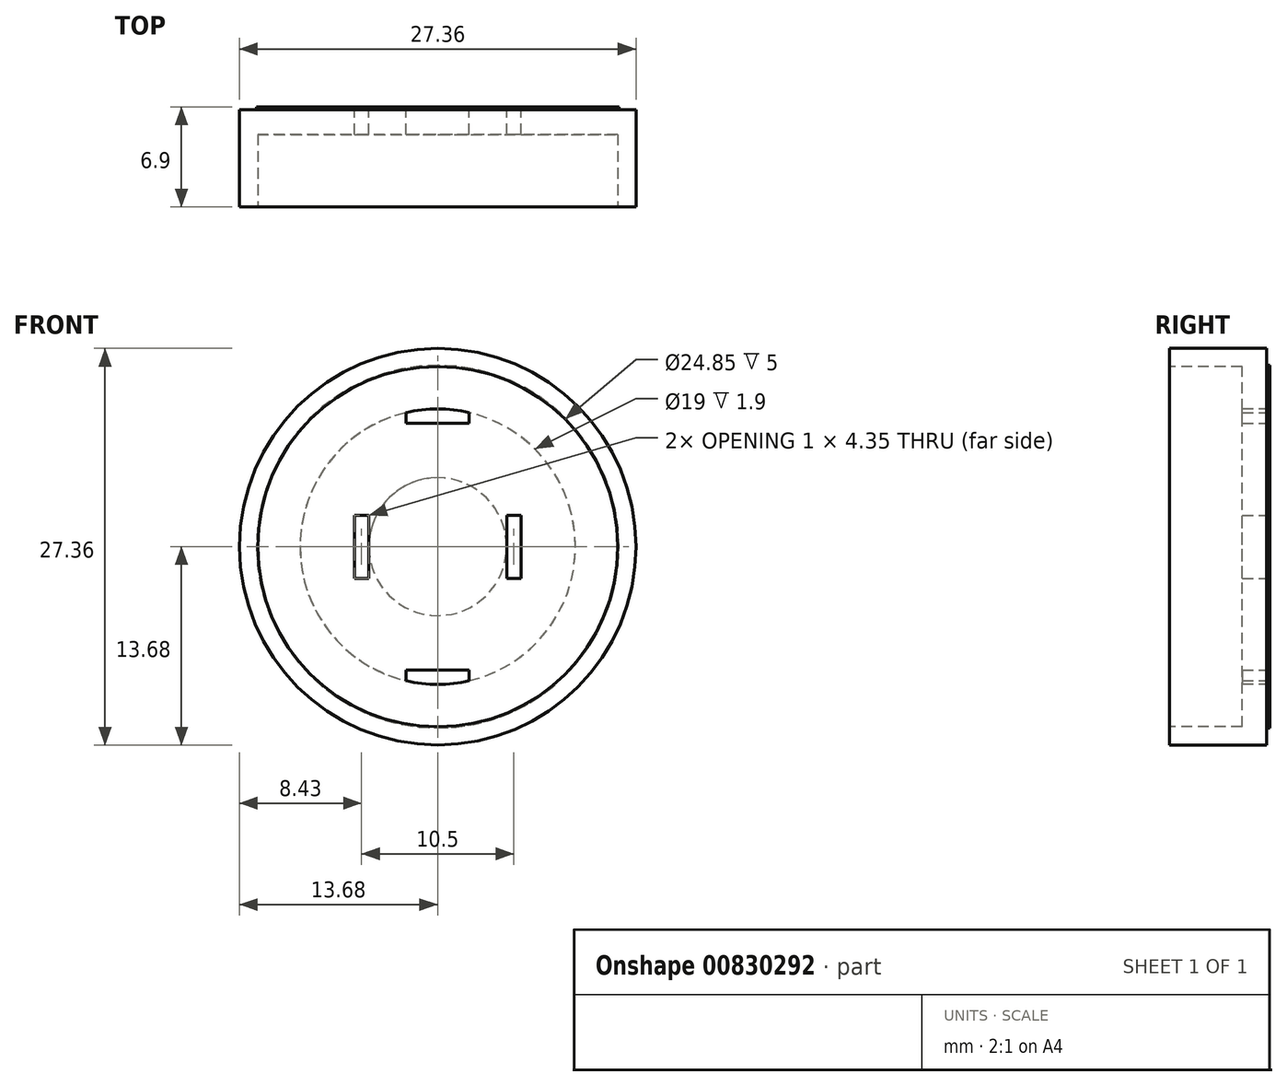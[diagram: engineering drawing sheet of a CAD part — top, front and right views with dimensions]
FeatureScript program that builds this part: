
annotation { "Feature Type Name" : "Feature", "Feature Type Description" : "" }
export const myFeature = defineFeature(function(context is Context, id is Id, definition is map)
    precondition{}
    {
        {
            var Q0;
            Q0=qCreatedBy(makeId("Front.planeOp"),FACE);
            var sketch = newSketch(context, id + "F0", { "sketchPlane" : qUnion([Q0])});
            skCircle(sketch, "E0", {"center": v(0, 0) * mm, "radius": 13.68 * mm});
            skSolve(sketch);
        }
        {
            var Q0;
            Q0 = qSketchRegion(id + "F0", true);
            extrude(context, id + "F1", {"entities" : qUnion([Q0]), "depth" : 6.7 * mm, "offsetDistance" : 25 * mm});
        }
        {
            var Q0;
            Q0=makeQuery(id+"F1.opExtrude","CAP_FACE",FACE,{"disambiguationData":[OSD([sQuery(id+"F0.wireOp",EDGE,"E0")])],"isStart":false});
            var sketch = newSketch(context, id + "F2", { "sketchPlane" : qUnion([Q0])});
            skCircle(sketch, "E1", {"center": v(0, 0) * mm, "radius": 12.43 * mm});
            skSolve(sketch);
        }
        {
            var Q0;
            Q0=makeQuery(id+"F2.imprint","IMPRINT",FACE,{"disambiguationData":[TD([[makeQuery(id+"F2.imprint","IMPRINT",EDGE,{"derivedFrom":sQuery(id+"F2.wireOp",EDGE,"E1")}),1.0]])]});
            extrude(context, id + "F3", {"entities" : qUnion([Q0]), "operationType" : NewBodyOperationType.REMOVE, "oppositeDirection" : true, "depth" : 5 * mm, "offsetDistance" : 25 * mm});
        }
        {
            var Q0;
            Q0=makeQuery(id+"F1.opExtrude","CAP_FACE",FACE,{"disambiguationData":[OSD([sQuery(id+"F0.wireOp",EDGE,"E0")])],"isStart":true});
            var sketch = newSketch(context, id + "F4", { "sketchPlane" : qUnion([Q0])});
            skCircle(sketch, "E2", {"center": v(0, 0) * mm, "radius": 4.75 * mm});
            skCircle(sketch, "E3", {"center": v(0, 0) * mm, "radius": 9.5 * mm});
            skCircle(sketch, "E4", {"center": v(0, 0) * mm, "radius": 12.5 * mm});
            skSolve(sketch);
        }
        {
            var Q0;
            Q0=makeQuery(id+"F4.imprint","IMPRINT",FACE,{"disambiguationData":[TD([[makeQuery(id+"F4.imprint","IMPRINT",EDGE,{"derivedFrom":sQuery(id+"F4.wireOp",EDGE,"E2")}),1.0]])]});
            extrude(context, id + "F5", {"entities" : qUnion([Q0]), "operationType" : NewBodyOperationType.ADD, "depth" : 0.2 * mm, "offsetDistance" : 25 * mm});
        }
        {
            var Q0;
            Q0=makeQuery(id+"F4.imprint","IMPRINT",FACE,{"disambiguationData":[TD([[makeQuery(id+"F4.imprint","IMPRINT",EDGE,{"derivedFrom":sQuery(id+"F4.wireOp",EDGE,"E3")}),-1.0]])]});
            extrude(context, id + "F6", {"entities" : qUnion([Q0]), "operationType" : NewBodyOperationType.ADD, "depth" : 0.2 * mm, "offsetDistance" : 25 * mm});
        }
        {
            var Q0;
            Q0=makeQuery(id+"F4.imprint","IMPRINT",FACE,{"disambiguationData":[TD([[makeQuery(id+"F4.imprint","IMPRINT",EDGE,{"derivedFrom":sQuery(id+"F4.wireOp",EDGE,"E2")}),-1.0]])]});
            var sketch = newSketch(context, id + "F7", { "sketchPlane" : qUnion([Q0])});
            skLineSegment(sketch, "E5.bottom", {"start": v(4.75, 2.17) * mm, "end": v(5.75, 2.17) * mm});
            skLineSegment(sketch, "E5.top", {"start": v(4.75, -2.17) * mm, "end": v(5.75, -2.17) * mm});
            skLineSegment(sketch, "E5.left", {"start": v(4.75, 2.17) * mm, "end": v(4.75, -2.17) * mm});
            skLineSegment(sketch, "E5.right", {"start": v(5.75, 2.17) * mm, "end": v(5.75, -2.17) * mm});
            skLineSegment(sketch, "E6.1.0", {"start": v(-4.75, -2.18) * mm, "end": v(-5.75, -2.18) * mm});
            skLineSegment(sketch, "E6.1.1", {"start": v(-4.75, -2.18) * mm, "end": v(-4.75, 2.17) * mm});
            skLineSegment(sketch, "E6.1.2", {"start": v(-5.75, -2.18) * mm, "end": v(-5.75, 2.17) * mm});
            skLineSegment(sketch, "E6.1.3", {"start": v(-4.75, 2.17) * mm, "end": v(-5.75, 2.17) * mm});
            skPoint(sketch, "E6.center", {"position": v(0, 0) * mm});
            skLineSegment(sketch, "E6.anchor1", {"start": v(0, 0) * mm, "end": v(4.75, 2.17) * mm, "construction": true});
            skLineSegment(sketch, "E6.anchor2", {"start": v(0, 0) * mm, "end": v(-4.75, -2.18) * mm, "construction": true});
            skSolve(sketch);
        }
        {
            var Q0;
            {var subQ3=sQuery(id+"F7.wireOp",EDGE,"E6.1.0");Q0=makeQuery(id+"F7.imprint","IMPRINT",FACE,{"disambiguationData":[TD([[makeQuery(id+"F7.imprint","IMPRINT",EDGE,{"derivedFrom":subQ3}),-1.0]])]});}
            var Q1;
            {var subQ3=sQuery(id+"F7.wireOp",EDGE,"E5.bottom");Q1=makeQuery(id+"F7.imprint","IMPRINT",FACE,{"disambiguationData":[TD([[makeQuery(id+"F7.imprint","IMPRINT",EDGE,{"derivedFrom":subQ3}),-1.0]])]});}
            var Q2;
            Q2=sQuery(id+"F7.wireOp",EDGE,"E6.1.2");
            var Q3;
            Q3=sQuery(id+"F7.wireOp",EDGE,"E6.1.1");
            var Q4;
            Q4=sQuery(id+"F7.wireOp",EDGE,"E6.1.3");
            var Q5;
            Q5=sQuery(id+"F7.wireOp",EDGE,"E6.1.0");
            var Q6;
            Q6=sQuery(id+"F7.wireOp",EDGE,"E5.top");
            var Q7;
            Q7=sQuery(id+"F7.wireOp",EDGE,"E5.right");
            var Q8;
            Q8=sQuery(id+"F7.wireOp",EDGE,"E5.left");
            var Q9;
            Q9=sQuery(id+"F7.wireOp",EDGE,"E5.bottom");
            extrude(context, id + "F8", {"entities" : qUnion([Q0, Q1]), "operationType" : NewBodyOperationType.REMOVE, "surfaceEntities" : qUnion([Q2, Q3, Q4, Q5, Q6, Q7, Q8, Q9]), "endBound" : BoundingType.THROUGH_ALL, "oppositeDirection" : true, "depth" : 25 * mm, "offsetDistance" : 25 * mm});
        }
        {
            var Q0;
            Q0=makeQuery(id+"F4.imprint","IMPRINT",FACE,{"disambiguationData":[TD([[makeQuery(id+"F4.imprint","IMPRINT",EDGE,{"derivedFrom":sQuery(id+"F4.wireOp",EDGE,"E2")}),-1.0]])]});
            var sketch = newSketch(context, id + "F9", { "sketchPlane" : qUnion([Q0])});
            skLineSegment(sketch, "E7.bottom", {"start": v(-2.17, 9.5) * mm, "end": v(2.17, 9.5) * mm});
            skLineSegment(sketch, "E7.top", {"start": v(-2.17, 8.5) * mm, "end": v(2.17, 8.5) * mm});
            skLineSegment(sketch, "E7.left", {"start": v(-2.18, 9.5) * mm, "end": v(-2.18, 8.5) * mm});
            skLineSegment(sketch, "E7.right", {"start": v(2.17, 9.5) * mm, "end": v(2.17, 8.5) * mm});
            skLineSegment(sketch, "E8.1.0", {"start": v(2.17, -8.5) * mm, "end": v(-2.17, -8.5) * mm});
            skLineSegment(sketch, "E8.1.1", {"start": v(-2.17, -9.5) * mm, "end": v(-2.17, -8.5) * mm});
            skLineSegment(sketch, "E8.1.2", {"start": v(2.17, -9.5) * mm, "end": v(-2.17, -9.5) * mm});
            skLineSegment(sketch, "E8.1.3", {"start": v(2.18, -9.5) * mm, "end": v(2.18, -8.5) * mm});
            skPoint(sketch, "E8.center", {"position": v(0, 0) * mm});
            skLineSegment(sketch, "E8.anchor1", {"start": v(0, 0) * mm, "end": v(-2.17, 8.5) * mm, "construction": true});
            skLineSegment(sketch, "E8.anchor2", {"start": v(0, 0) * mm, "end": v(2.18, -8.5) * mm, "construction": true});
            skSolve(sketch);
        }
        {
            var Q0;
            {var subQ1=sQuery(id+"F9.wireOp",EDGE,"E8.1.0");Q0=makeQuery(id+"F9.imprint","IMPRINT",FACE,{"disambiguationData":[TD([[makeQuery(id+"F9.imprint","IMPRINT",EDGE,{"derivedFrom":subQ1}),1.0]])]});}
            var Q1;
            {var subQ1=sQuery(id+"F9.wireOp",EDGE,"E7.top");Q1=makeQuery(id+"F9.imprint","IMPRINT",FACE,{"disambiguationData":[TD([[makeQuery(id+"F9.imprint","IMPRINT",EDGE,{"derivedFrom":subQ1}),1.0]])]});}
            var Q2;
            Q2=sQuery(id+"F9.wireOp",EDGE,"E7.top");
            var Q3;
            Q3=sQuery(id+"F9.wireOp",EDGE,"E7.right");
            var Q4;
            Q4=sQuery(id+"F9.wireOp",EDGE,"E7.bottom");
            var Q5;
            Q5=sQuery(id+"F9.wireOp",EDGE,"E7.left");
            var Q6;
            Q6=sQuery(id+"F9.wireOp",EDGE,"E8.1.0");
            var Q7;
            Q7=sQuery(id+"F9.wireOp",EDGE,"E8.1.3");
            var Q8;
            Q8=sQuery(id+"F9.wireOp",EDGE,"E8.1.1");
            var Q9;
            Q9=sQuery(id+"F9.wireOp",EDGE,"E8.1.2");
            extrude(context, id + "F10", {"entities" : qUnion([Q0, Q1]), "operationType" : NewBodyOperationType.REMOVE, "surfaceEntities" : qUnion([Q2, Q3, Q4, Q5, Q6, Q7, Q8, Q9]), "endBound" : BoundingType.THROUGH_ALL, "oppositeDirection" : true, "depth" : 25 * mm, "offsetDistance" : 25 * mm});
        }
    });
